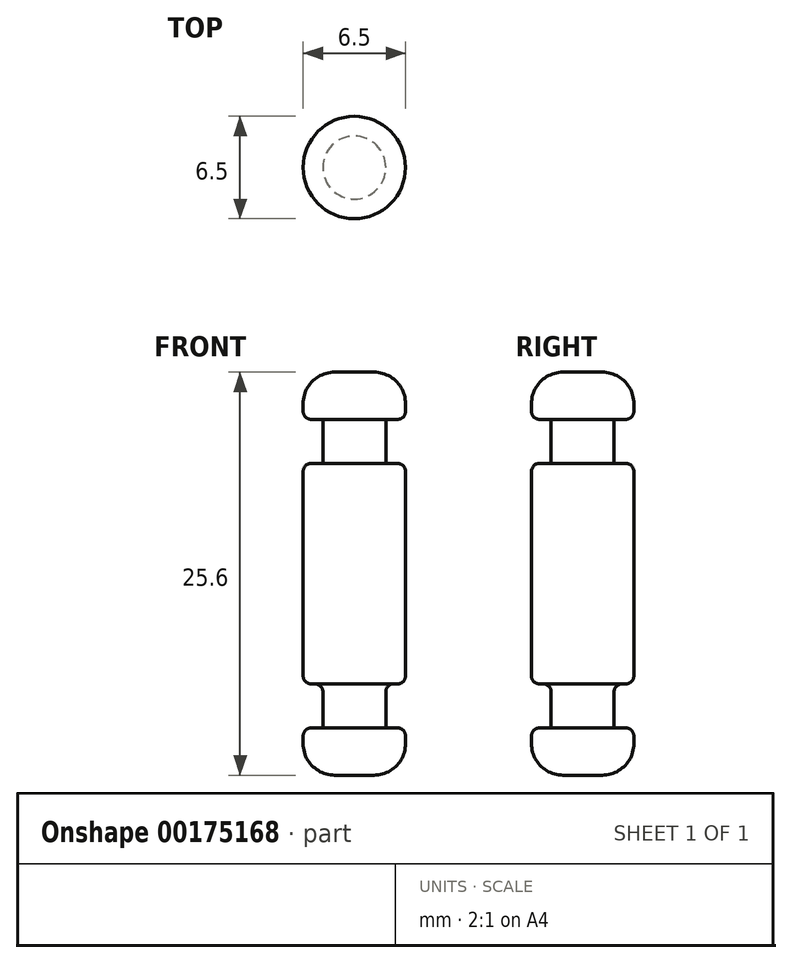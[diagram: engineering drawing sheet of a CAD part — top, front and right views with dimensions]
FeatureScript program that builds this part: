
annotation { "Feature Type Name" : "Feature", "Feature Type Description" : "" }
export const myFeature = defineFeature(function(context is Context, id is Id, definition is map)
    precondition{}
    {
        {
            var Q0;
            Q0=qCreatedBy(makeId("Top.planeOp"),FACE);
            var sketch = newSketch(context, id + "F0", { "sketchPlane" : qUnion([Q0])});
            skCircle(sketch, "E0", {"center": v(0, 0) * mm, "radius": 3.25 * mm});
            skCircle(sketch, "E1", {"center": v(0, 0) * mm, "radius": 2 * mm});
            skSolve(sketch);
        }
        {
            var Q0;
            Q0=makeQuery(id+"F0.imprint","IMPRINT",FACE,{"disambiguationData":[TD([[makeQuery(id+"F0.imprint","IMPRINT",EDGE,{"derivedFrom":sQuery(id+"F0.wireOp",EDGE,"E1")}),1.0]])]});
            extrude(context, id + "F1", {"entities" : qUnion([Q0]), "depth" : 9.8 * mm, "hasSecondDirection" : true, "secondDirectionOppositeDirection" : true, "secondDirectionDepth" : 9.8 * mm});
        }
        {
            var Q0;
            Q0 = qSketchRegion(id + "F0", true);
            extrude(context, id + "F2", {"entities" : qUnion([Q0]), "operationType" : NewBodyOperationType.ADD, "depth" : 7 * mm, "hasSecondDirection" : true, "secondDirectionOppositeDirection" : true, "secondDirectionDepth" : 7 * mm});
        }
        {
            var Q0;
            Q0=makeQuery(id+"F1.opExtrude","CAP_FACE",FACE,{"disambiguationData":[OSD([sQuery(id+"F0.wireOp",EDGE,"E1")])],"isStart":true});
            var sketch = newSketch(context, id + "F3", { "sketchPlane" : qUnion([Q0])});
            skCircle(sketch, "E2", {"center": v(0, 0) * mm, "radius": 3.25 * mm});
            skSolve(sketch);
        }
        {
            var Q0;
            Q0=makeQuery(id+"F1.opExtrude","CAP_FACE",FACE,{"disambiguationData":[OSD([sQuery(id+"F0.wireOp",EDGE,"E1")])],"isStart":false});
            var sketch = newSketch(context, id + "F4", { "sketchPlane" : qUnion([Q0])});
            skCircle(sketch, "E3", {"center": v(0, 0) * mm, "radius": 3.25 * mm});
            skSolve(sketch);
        }
        {
            var Q0;
            Q0 = qSketchRegion(id + "F4", true);
            extrude(context, id + "F5", {"entities" : qUnion([Q0]), "operationType" : NewBodyOperationType.ADD, "depth" : 3 * mm});
        }
        {
            var Q0;
            Q0 = qSketchRegion(id + "F3", true);
            extrude(context, id + "F6", {"entities" : qUnion([Q0]), "operationType" : NewBodyOperationType.ADD, "depth" : 3 * mm});
        }
        {
            var Q0;
            Q0=makeQuery(id+"F5.opExtrude","CAP_EDGE",EDGE,{"disambiguationData":[OSD([sQuery(id+"F4.wireOp",EDGE,"E3")])],"isStart":false});
            var Q1;
            Q1=makeQuery(id+"F6.opExtrude","CAP_EDGE",EDGE,{"disambiguationData":[OSD([sQuery(id+"F3.wireOp",EDGE,"E2")])],"isStart":false});
            fillet(context, id + "F7", {"entities" : qUnion([Q0, Q1]), "radius" : 2 * mm, "tangentPropagation" : true, "allowEdgeOverflow" : false});
        }
        {
            var Q0;
            {var subQ0=sQuery(id+"F4.wireOp",EDGE,"E3");Q0=makeQuery(id+"F7.opFillet","BLEND_EDGE",EDGE,{"blendedFrom":[makeQuery(id+"F5.opExtrude","CAP_EDGE",EDGE,{"disambiguationData":[OSD([subQ0])],"isStart":false}),makeQuery(id+"F5.opExtrude","CAP_FACE",FACE,{"disambiguationData":[OSD([subQ0])],"isStart":true})],"blendedInto":[makeQuery(id+"F5.opExtrude","CAP_FACE",FACE,{"disambiguationData":[OSD([subQ0])],"isStart":true})]});}
            var Q1;
            Q1=makeQuery(id+"F2.opExtrude","CAP_EDGE",EDGE,{"disambiguationData":[OSD([sQuery(id+"F0.wireOp",EDGE,"E0")])],"isStart":false});
            var Q2;
            Q2=makeQuery(id+"F2.opExtrude","CAP_EDGE",EDGE,{"disambiguationData":[OSD([sQuery(id+"F0.wireOp",EDGE,"E0")])],"isStart":true});
            var Q3;
            {var subQ0=sQuery(id+"F3.wireOp",EDGE,"E2");Q3=makeQuery(id+"F7.opFillet","BLEND_EDGE",EDGE,{"blendedFrom":[makeQuery(id+"F6.opExtrude","CAP_EDGE",EDGE,{"disambiguationData":[OSD([subQ0])],"isStart":false}),makeQuery(id+"F6.opExtrude","CAP_FACE",FACE,{"disambiguationData":[OSD([subQ0])],"isStart":true})],"blendedInto":[makeQuery(id+"F6.opExtrude","CAP_FACE",FACE,{"disambiguationData":[OSD([subQ0])],"isStart":true})]});}
            var Q4;
            Q4=makeQuery(id+"F1.opExtrude","CAP_EDGE",EDGE,{"disambiguationData":[OSD([sQuery(id+"F0.wireOp",EDGE,"E1")])],"isStart":true});
            var Q5;
            Q5=makeQuery(id+"F2.opExtrude","CAP_EDGE",EDGE,{"disambiguationData":[OSD([sQuery(id+"F0.wireOp",EDGE,"E1")])],"isStart":true});
            var Q6;
            Q6=makeQuery(id+"F1.opExtrude","CAP_EDGE",EDGE,{"disambiguationData":[OSD([sQuery(id+"F0.wireOp",EDGE,"E1")])],"isStart":false});
            var Q7;
            Q7=makeQuery(id+"F2.opExtrude","CAP_EDGE",EDGE,{"disambiguationData":[OSD([sQuery(id+"F0.wireOp",EDGE,"E1")])],"isStart":false});
            var Q8;
            Q8=makeQuery(id+"F5.opExtrude","CAP_EDGE",EDGE,{"disambiguationData":[OSD([sQuery(id+"F4.wireOp",EDGE,"E3")])],"isStart":true});
            var Q9;
            Q9=makeQuery(id+"F6.opExtrude","CAP_EDGE",EDGE,{"disambiguationData":[OSD([sQuery(id+"F3.wireOp",EDGE,"E2")])],"isStart":true});
            fillet(context, id + "F8", {"entities" : qUnion([Q0, Q1, Q2, Q3, Q4, Q5, Q6, Q7, Q8, Q9]), "radius" : .5 * mm, "tangentPropagation" : true, "allowEdgeOverflow" : false});
        }
    });
